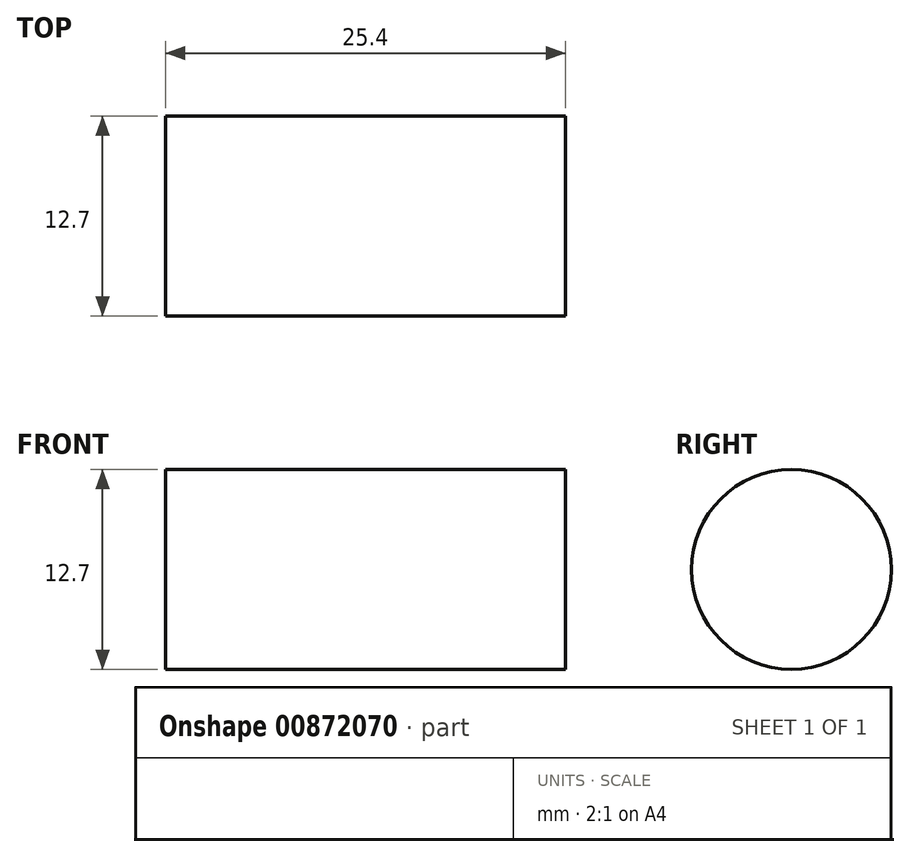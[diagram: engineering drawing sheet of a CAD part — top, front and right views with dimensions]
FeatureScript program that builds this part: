
annotation { "Feature Type Name" : "Feature", "Feature Type Description" : "" }
export const myFeature = defineFeature(function(context is Context, id is Id, definition is map)
    precondition{}
    {
        {
            var Q0;
            Q0=qCreatedBy(makeId("Right.planeOp"),FACE);
            var sketch = newSketch(context, id + "F0", { "sketchPlane" : qUnion([Q0])});
            skCircle(sketch, "E0", {"center": v(0, 0) * mm, "radius": 6.35 * mm});
            skSolve(sketch);
        }
        {
            var Q0;
            Q0 = qSketchRegion(id + "F0", true);
            extrude(context, id + "F1", {"entities" : qUnion([Q0]), "depth" : 25.4 * mm, "offsetDistance" : 25.4 * mm});
        }
    });
